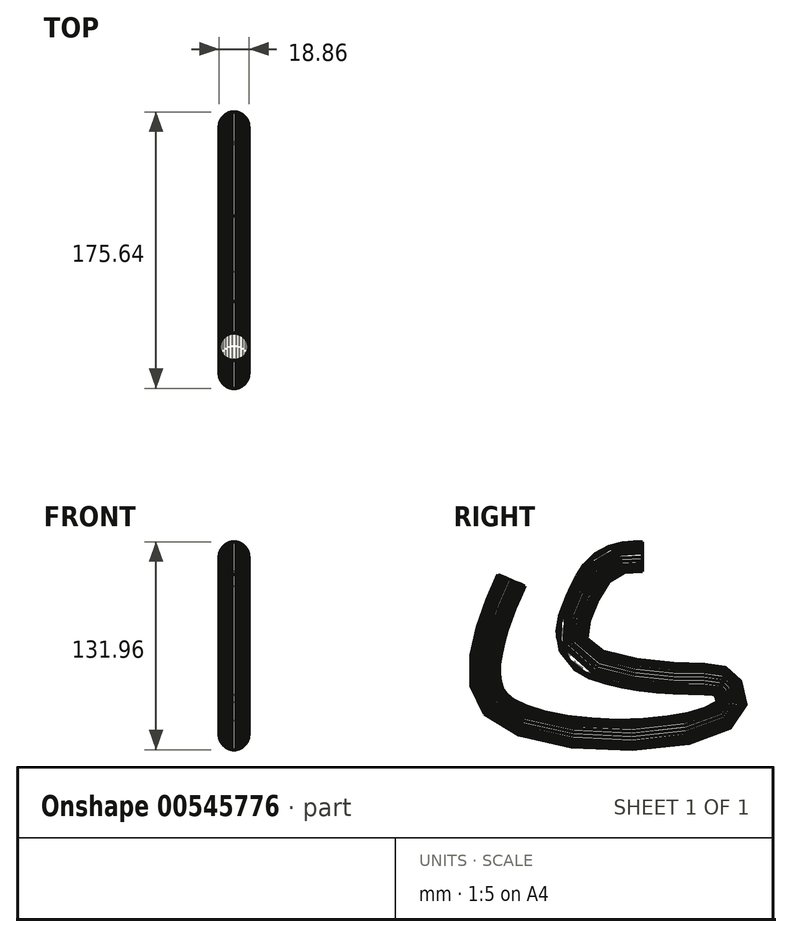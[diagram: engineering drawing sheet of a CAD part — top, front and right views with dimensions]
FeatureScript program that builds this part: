
annotation { "Feature Type Name" : "Feature", "Feature Type Description" : "" }
export const myFeature = defineFeature(function(context is Context, id is Id, definition is map)
    precondition{}
    {
        {
            var Q0;
            Q0=qCreatedBy(makeId("Front.planeOp"),FACE);
            var sketch = newSketch(context, id + "F0", { "sketchPlane" : qUnion([Q0])});
            skCircle(sketch, "E0.cCircle", {"center": v(39.7, 45.3) * mm, "radius": 9.36 * mm, "construction": true});
            skLineSegment(sketch, "E0.0", {"start": v(40.83, 35.95) * mm, "end": v(38.55, 35.95) * mm});
            skLineSegment(sketch, "E0.1", {"start": v(38.55, 35.95) * mm, "end": v(36.35, 36.5) * mm});
            skLineSegment(sketch, "E0.2", {"start": v(36.35, 36.5) * mm, "end": v(34.33, 37.55) * mm});
            skLineSegment(sketch, "E0.3", {"start": v(34.33, 37.55) * mm, "end": v(32.63, 39.05) * mm});
            skLineSegment(sketch, "E0.4", {"start": v(32.63, 39.05) * mm, "end": v(31.34, 40.92) * mm});
            skLineSegment(sketch, "E0.5", {"start": v(31.34, 40.92) * mm, "end": v(30.53, 43.05) * mm});
            skLineSegment(sketch, "E0.6", {"start": v(30.53, 43.05) * mm, "end": v(30.26, 45.3) * mm});
            skLineSegment(sketch, "E0.7", {"start": v(30.26, 45.3) * mm, "end": v(30.53, 47.56) * mm});
            skLineSegment(sketch, "E0.8", {"start": v(30.53, 47.56) * mm, "end": v(31.34, 49.69) * mm});
            skLineSegment(sketch, "E0.9", {"start": v(31.34, 49.69) * mm, "end": v(32.63, 51.56) * mm});
            skLineSegment(sketch, "E0.10", {"start": v(32.63, 51.56) * mm, "end": v(34.33, 53.07) * mm});
            skLineSegment(sketch, "E0.11", {"start": v(34.33, 53.07) * mm, "end": v(36.35, 54.12) * mm});
            skLineSegment(sketch, "E0.12", {"start": v(36.35, 54.12) * mm, "end": v(38.55, 54.67) * mm});
            skLineSegment(sketch, "E0.13", {"start": v(38.55, 54.67) * mm, "end": v(40.83, 54.67) * mm});
            skLineSegment(sketch, "E0.14", {"start": v(40.83, 54.67) * mm, "end": v(43.03, 54.12) * mm});
            skLineSegment(sketch, "E0.15", {"start": v(43.03, 54.12) * mm, "end": v(45.05, 53.07) * mm});
            skLineSegment(sketch, "E0.16", {"start": v(45.05, 53.07) * mm, "end": v(46.75, 51.56) * mm});
            skLineSegment(sketch, "E0.17", {"start": v(46.75, 51.56) * mm, "end": v(48.04, 49.69) * mm});
            skLineSegment(sketch, "E0.18", {"start": v(48.04, 49.69) * mm, "end": v(48.85, 47.56) * mm});
            skLineSegment(sketch, "E0.19", {"start": v(48.85, 47.56) * mm, "end": v(49.12, 45.3) * mm});
            skLineSegment(sketch, "E0.20", {"start": v(49.12, 45.3) * mm, "end": v(48.85, 43.05) * mm});
            skLineSegment(sketch, "E0.21", {"start": v(48.85, 43.05) * mm, "end": v(48.04, 40.92) * mm});
            skLineSegment(sketch, "E0.22", {"start": v(48.04, 40.92) * mm, "end": v(46.75, 39.05) * mm});
            skLineSegment(sketch, "E0.23", {"start": v(46.75, 39.05) * mm, "end": v(45.05, 37.55) * mm});
            skLineSegment(sketch, "E0.24", {"start": v(45.05, 37.55) * mm, "end": v(43.03, 36.5) * mm});
            skLineSegment(sketch, "E0.25", {"start": v(43.03, 36.5) * mm, "end": v(40.83, 35.95) * mm});
            skPoint(sketch, "E0.0.midPoint", {"position": v(39.7, 35.95) * mm});
            skSolve(sketch);
        }
        {
            var Q0;
            Q0=qCreatedBy(makeId("Right.planeOp"),FACE);
            var sketch = newSketch(context, id + "F1", { "sketchPlane" : qUnion([Q0])});
            skFitSpline(sketch, "E1", {"points": [v(0, 35.57) * mm, v(-17.97, 32.2) * mm, v(-31.45, 9.36) * mm, v(-32.95, -9.36) * mm, v(28.46, -22.47) * mm, v(58.41, -28.08) * mm, v(61.03, -59.91) * mm, v(-90.61, -62.53) * mm, v(-108.21, -11.6) * mm, v(-92.11, 34.07) * mm], "startDerivative": vector(-270.76, 5.27) * mm, "endDerivative": vector(164.23, 369.29) * mm});
            skSolve(sketch);
        }
        {
            var Q0;
            Q0=makeQuery(id+"F0.imprint","IMPRINT",FACE,{"disambiguationData":[TD([[makeQuery(id+"F0.imprint","IMPRINT",EDGE,{"derivedFrom":sQuery(id+"F0.wireOp",EDGE,"E0.0")}),-1.0]])]});
            var Q1;
            Q1=sQuery(id+"F1.wireOp",EDGE,"E1");
            sweep(context, id + "F2", {"profiles" : qUnion([Q0]), "path" : qUnion([Q1])});
        }
    });
